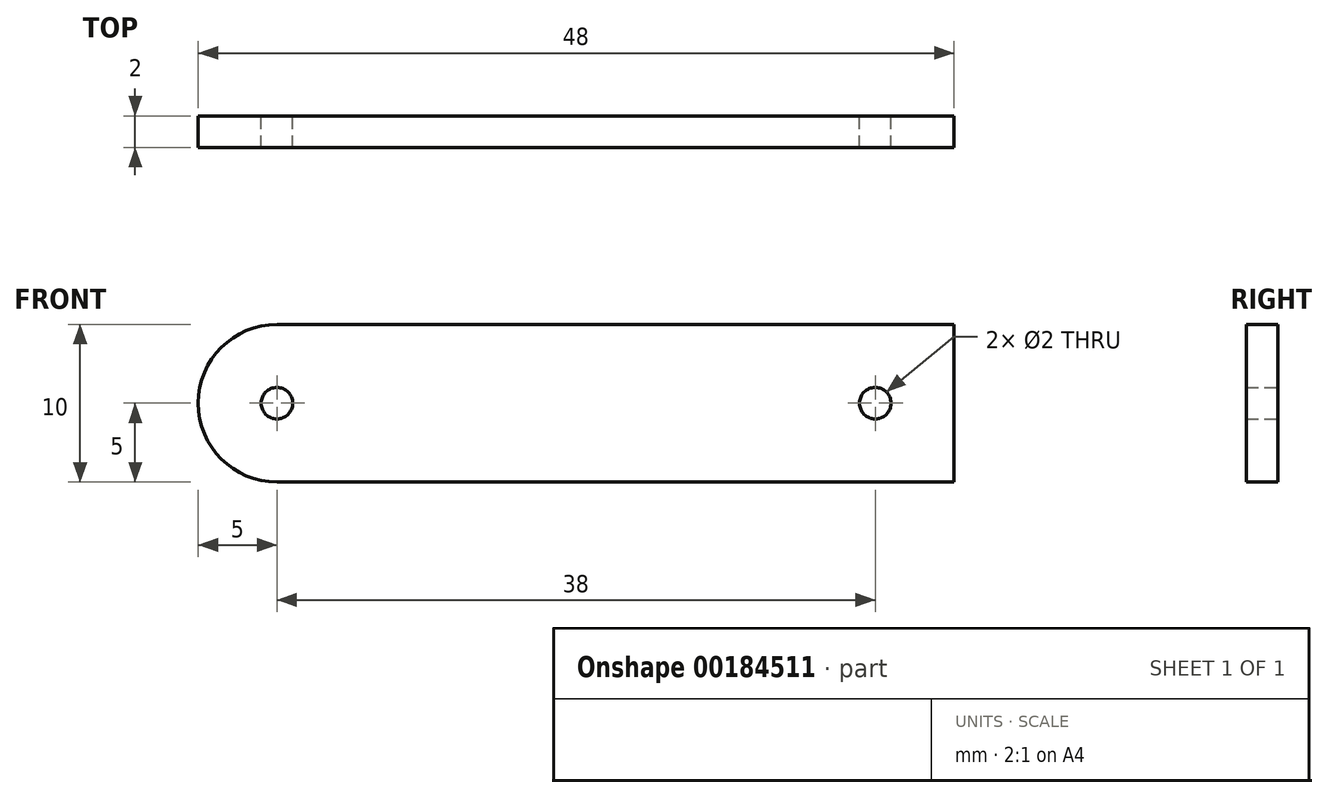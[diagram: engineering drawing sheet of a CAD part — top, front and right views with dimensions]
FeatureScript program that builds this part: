
annotation { "Feature Type Name" : "Feature", "Feature Type Description" : "" }
export const myFeature = defineFeature(function(context is Context, id is Id, definition is map)
    precondition{}
    {
        {
            var Q0;
            Q0=qCreatedBy(makeId("Front.planeOp"),FACE);
            var sketch = newSketch(context, id + "F0", { "sketchPlane" : qUnion([Q0])});
            skLineSegment(sketch, "E0.bottom", {"start": v(0, 0) * mm, "end": v(48, 0) * mm});
            skLineSegment(sketch, "E0.top", {"start": v(0, -10) * mm, "end": v(48, -10) * mm});
            skLineSegment(sketch, "E0.left", {"start": v(0, 0) * mm, "end": v(0, -10) * mm});
            skLineSegment(sketch, "E0.right", {"start": v(48, 0) * mm, "end": v(48, -10) * mm});
            skCircle(sketch, "E1", {"center": v(5, -5) * mm, "radius": 1 * mm});
            skCircle(sketch, "E2", {"center": v(43, -5) * mm, "radius": 1 * mm});
            skSolve(sketch);
        }
        {
            var Q0;
            Q0 = qSketchRegion(id + "F0", true);
            extrude(context, id + "F1", {"entities" : qUnion([Q0]), "depth" : 2 * mm});
        }
        {
            var Q0;
            Q0=makeQuery(id+"F1.opExtrude","SWEPT_EDGE",EDGE,{"disambiguationData":[OSD([sQuery(id+"F0.wireOp",EDGE,"E0.bottom"),sQuery(id+"F0.wireOp",EDGE,"E0.left")])]});
            var Q1;
            Q1=makeQuery(id+"F1.opExtrude","SWEPT_EDGE",EDGE,{"disambiguationData":[OSD([sQuery(id+"F0.wireOp",EDGE,"E0.top"),sQuery(id+"F0.wireOp",EDGE,"E0.left")])]});
            fillet(context, id + "F2", {"entities" : qUnion([Q0, Q1]), "radius" : 5 * mm, "tangentPropagation" : true, "allowEdgeOverflow" : false});
        }
    });
